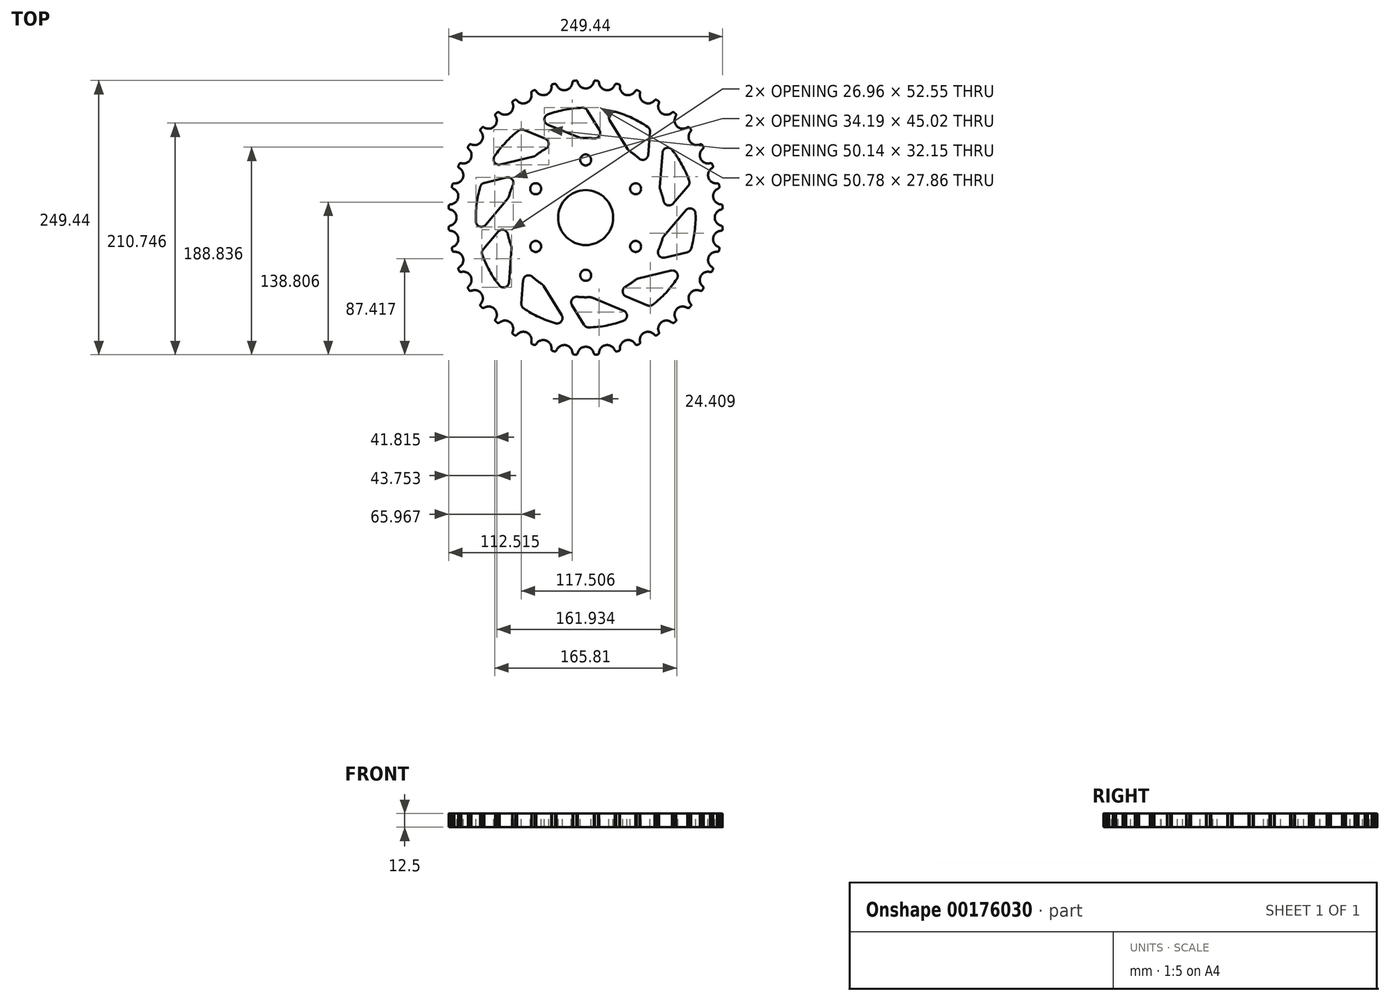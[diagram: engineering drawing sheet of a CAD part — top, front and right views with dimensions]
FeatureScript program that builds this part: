
annotation { "Feature Type Name" : "Feature", "Feature Type Description" : "" }
export const myFeature = defineFeature(function(context is Context, id is Id, definition is map)
    precondition{}
    {
        {
            var Q0;
            Q0=qCreatedBy(makeId("Top.planeOp"),FACE);
            var sketch = newSketch(context, id + "F0", { "sketchPlane" : qUnion([Q0])});
            skCircle(sketch, "E0", {"center": v(0, 0) * mm, "radius": 125 * mm});
            skSolve(sketch);
        }
        {
            var Q0;
            Q0 = qSketchRegion(id + "F0", true);
            extrude(context, id + "F1", {"entities" : qUnion([Q0]), "depth" : 12.5 * mm});
        }
        {
            var Q0;
            Q0=makeQuery(id+"F1.opExtrude","CAP_FACE",FACE,{"disambiguationData":[OSD([sQuery(id+"F0.wireOp",EDGE,"E0")])],"isStart":false});
            var sketch = newSketch(context, id + "F2", { "sketchPlane" : qUnion([Q0])});
            skCircle(sketch, "E1", {"center": v(0, 0) * mm, "radius": 25 * mm});
            skSolve(sketch);
        }
        {
            var Q0;
            Q0 = qSketchRegion(id + "F2", true);
            extrude(context, id + "F3", {"entities" : qUnion([Q0]), "operationType" : NewBodyOperationType.REMOVE, "endBound" : BoundingType.THROUGH_ALL, "oppositeDirection" : true, "depth" : 25 * mm});
        }
        {
            var Q0;
            Q0=makeQuery(id+"F1.opExtrude","CAP_FACE",FACE,{"disambiguationData":[OSD([sQuery(id+"F0.wireOp",EDGE,"E0")])],"isStart":false});
            var sketch = newSketch(context, id + "F4", { "sketchPlane" : qUnion([Q0])});
            skArc(sketch, "E2", {"start": v(-42.76, 30.46) * mm, "mid": v(-45.47, 26.25) * mm, "end": v(-47.76, 21.8) * mm});
            skCircle(sketch, "E3", {"center": v(0, 52.5) * mm, "radius": 5 * mm});
            skCircle(sketch, "E4.1.0", {"center": v(-45.47, 26.25) * mm, "radius": 5 * mm});
            skCircle(sketch, "E4.2.0", {"center": v(-45.47, -26.25) * mm, "radius": 5 * mm});
            skCircle(sketch, "E4.3.0", {"center": v(0, -52.5) * mm, "radius": 5 * mm});
            skCircle(sketch, "E4.4.0", {"center": v(45.47, -26.25) * mm, "radius": 5 * mm});
            skCircle(sketch, "E4.5.0", {"center": v(45.47, 26.25) * mm, "radius": 5 * mm});
            skArc(sketch, "E5.trimOffspring", {"start": v(5, 52.26) * mm, "mid": v(0, 52.5) * mm, "end": v(-5, 52.26) * mm});
            skArc(sketch, "E6.trimOffspring", {"start": v(-47.76, -21.8) * mm, "mid": v(-45.47, -26.25) * mm, "end": v(-42.76, -30.46) * mm});
            skArc(sketch, "E7.trimOffspring", {"start": v(47.76, 21.8) * mm, "mid": v(45.47, 26.25) * mm, "end": v(42.76, 30.46) * mm});
            skArc(sketch, "E8.trimOffspring", {"start": v(42.76, -30.46) * mm, "mid": v(45.47, -26.25) * mm, "end": v(47.76, -21.8) * mm});
            skArc(sketch, "E9.trimOffspring", {"start": v(-5, -52.26) * mm, "mid": v(0, -52.5) * mm, "end": v(5, -52.26) * mm});
            skSolve(sketch);
        }
        {
            var Q0;
            Q0 = qSketchRegion(id + "F4", true);
            extrude(context, id + "F5", {"entities" : qUnion([Q0]), "operationType" : NewBodyOperationType.REMOVE, "endBound" : BoundingType.THROUGH_ALL, "oppositeDirection" : true, "depth" : 25 * mm});
        }
        {
            var Q0;
            Q0=makeQuery(id+"F1.opExtrude","CAP_FACE",FACE,{"disambiguationData":[OSD([sQuery(id+"F0.wireOp",EDGE,"E0")])],"isStart":false});
            var sketch = newSketch(context, id + "F6", { "sketchPlane" : qUnion([Q0])});
            skCircle(sketch, "E10", {"center": v(0, 125) * mm, "radius": 7.5 * mm});
            skCircle(sketch, "E11.1.0", {"center": v(-19.55, 123.46) * mm, "radius": 7.5 * mm});
            skCircle(sketch, "E11.2.0", {"center": v(-38.63, 118.88) * mm, "radius": 7.5 * mm});
            skCircle(sketch, "E11.3.0", {"center": v(-56.75, 111.38) * mm, "radius": 7.5 * mm});
            skCircle(sketch, "E11.4.0", {"center": v(-73.47, 101.13) * mm, "radius": 7.5 * mm});
            skCircle(sketch, "E11.5.0", {"center": v(-88.39, 88.39) * mm, "radius": 7.5 * mm});
            skCircle(sketch, "E11.6.0", {"center": v(-101.13, 73.47) * mm, "radius": 7.5 * mm});
            skCircle(sketch, "E11.7.0", {"center": v(-111.38, 56.75) * mm, "radius": 7.5 * mm});
            skCircle(sketch, "E11.8.0", {"center": v(-118.88, 38.63) * mm, "radius": 7.5 * mm});
            skCircle(sketch, "E11.9.0", {"center": v(-123.46, 19.55) * mm, "radius": 7.5 * mm});
            skCircle(sketch, "E11.10.0", {"center": v(-125, 0) * mm, "radius": 7.5 * mm});
            skCircle(sketch, "E11.11.0", {"center": v(-123.46, -19.55) * mm, "radius": 7.5 * mm});
            skCircle(sketch, "E11.12.0", {"center": v(-118.88, -38.63) * mm, "radius": 7.5 * mm});
            skCircle(sketch, "E11.13.0", {"center": v(-111.38, -56.75) * mm, "radius": 7.5 * mm});
            skCircle(sketch, "E11.14.0", {"center": v(-101.13, -73.47) * mm, "radius": 7.5 * mm});
            skCircle(sketch, "E11.15.0", {"center": v(-88.39, -88.39) * mm, "radius": 7.5 * mm});
            skCircle(sketch, "E11.16.0", {"center": v(-73.47, -101.13) * mm, "radius": 7.5 * mm});
            skCircle(sketch, "E11.17.0", {"center": v(-56.75, -111.38) * mm, "radius": 7.5 * mm});
            skCircle(sketch, "E11.18.0", {"center": v(-38.63, -118.88) * mm, "radius": 7.5 * mm});
            skCircle(sketch, "E11.19.0", {"center": v(-19.55, -123.46) * mm, "radius": 7.5 * mm});
            skCircle(sketch, "E11.20.0", {"center": v(0, -125) * mm, "radius": 7.5 * mm});
            skCircle(sketch, "E11.21.0", {"center": v(19.55, -123.46) * mm, "radius": 7.5 * mm});
            skCircle(sketch, "E11.22.0", {"center": v(38.63, -118.88) * mm, "radius": 7.5 * mm});
            skCircle(sketch, "E11.23.0", {"center": v(56.75, -111.38) * mm, "radius": 7.5 * mm});
            skCircle(sketch, "E11.24.0", {"center": v(73.47, -101.13) * mm, "radius": 7.5 * mm});
            skCircle(sketch, "E11.25.0", {"center": v(88.39, -88.39) * mm, "radius": 7.5 * mm});
            skCircle(sketch, "E11.26.0", {"center": v(101.13, -73.47) * mm, "radius": 7.5 * mm});
            skCircle(sketch, "E11.27.0", {"center": v(111.38, -56.75) * mm, "radius": 7.5 * mm});
            skCircle(sketch, "E11.28.0", {"center": v(118.88, -38.63) * mm, "radius": 7.5 * mm});
            skCircle(sketch, "E11.29.0", {"center": v(123.46, -19.55) * mm, "radius": 7.5 * mm});
            skCircle(sketch, "E11.30.0", {"center": v(125, 0) * mm, "radius": 7.5 * mm});
            skCircle(sketch, "E11.31.0", {"center": v(123.46, 19.55) * mm, "radius": 7.5 * mm});
            skCircle(sketch, "E11.32.0", {"center": v(118.88, 38.63) * mm, "radius": 7.5 * mm});
            skCircle(sketch, "E11.33.0", {"center": v(111.38, 56.75) * mm, "radius": 7.5 * mm});
            skCircle(sketch, "E11.34.0", {"center": v(101.13, 73.47) * mm, "radius": 7.5 * mm});
            skCircle(sketch, "E11.35.0", {"center": v(88.39, 88.39) * mm, "radius": 7.5 * mm});
            skCircle(sketch, "E11.36.0", {"center": v(73.47, 101.13) * mm, "radius": 7.5 * mm});
            skCircle(sketch, "E11.37.0", {"center": v(56.75, 111.38) * mm, "radius": 7.5 * mm});
            skCircle(sketch, "E11.38.0", {"center": v(38.63, 118.88) * mm, "radius": 7.5 * mm});
            skCircle(sketch, "E11.39.0", {"center": v(19.55, 123.46) * mm, "radius": 7.5 * mm});
            skPoint(sketch, "E11.center", {"position": v(0, 0) * mm});
            skSolve(sketch);
        }
        {
            var Q0;
            Q0 = qSketchRegion(id + "F6", true);
            extrude(context, id + "F7", {"entities" : qUnion([Q0]), "operationType" : NewBodyOperationType.REMOVE, "endBound" : BoundingType.THROUGH_ALL, "oppositeDirection" : true, "depth" : 25 * mm});
        }
        {
            var Q0;
            Q0=makeQuery(id+"F1.opExtrude","CAP_FACE",FACE,{"disambiguationData":[OSD([sQuery(id+"F0.wireOp",EDGE,"E0")])],"isStart":false});
            var sketch = newSketch(context, id + "F8", { "sketchPlane" : qUnion([Q0])});
            skArc(sketch, "E12", {"start": v(8.47, 124.7) * mm, "mid": v(7.71, 124.13) * mm, "end": v(7.3, 123.29) * mm});
            skArc(sketch, "E13", {"start": v(12.07, 122.91) * mm, "mid": v(11.8, 123.81) * mm, "end": v(11.15, 124.49) * mm});
            skPoint(sketch, "E14.orphan", {"position": v(7.38, 123.29) * mm});
            skLineSegment(sketch, "E15", {"start": v(8.47, 124.7) * mm, "end": v(7.23, 125.28) * mm});
            skLineSegment(sketch, "E16", {"start": v(7.23, 125.28) * mm, "end": v(7.3, 123.29) * mm});
            skLineSegment(sketch, "E17", {"start": v(11.15, 124.49) * mm, "end": v(12.69, 124.92) * mm});
            skLineSegment(sketch, "E18", {"start": v(12.69, 124.92) * mm, "end": v(12.07, 122.91) * mm});
            skArc(sketch, "E19.1.0", {"start": v(-11.15, 124.49) * mm, "mid": v(-11.8, 123.81) * mm, "end": v(-12.07, 122.91) * mm});
            skLineSegment(sketch, "E19.1.1", {"start": v(-12.46, 124.87) * mm, "end": v(-12.07, 122.91) * mm});
            skLineSegment(sketch, "E19.1.2", {"start": v(-11.15, 124.49) * mm, "end": v(-12.46, 124.87) * mm});
            skLineSegment(sketch, "E19.1.3", {"start": v(-8.47, 124.7) * mm, "end": v(-7, 125.36) * mm});
            skArc(sketch, "E19.1.4", {"start": v(-7.3, 123.29) * mm, "mid": v(-7.71, 124.13) * mm, "end": v(-8.47, 124.7) * mm});
            skLineSegment(sketch, "E19.1.5", {"start": v(-7, 125.36) * mm, "end": v(-7.3, 123.29) * mm});
            skArc(sketch, "E19.2.0", {"start": v(-30.48, 121.21) * mm, "mid": v(-31.02, 120.44) * mm, "end": v(-31.15, 119.5) * mm});
            skLineSegment(sketch, "E19.2.1", {"start": v(-31.84, 121.38) * mm, "end": v(-31.15, 119.5) * mm});
            skLineSegment(sketch, "E19.2.2", {"start": v(-30.48, 121.21) * mm, "end": v(-31.84, 121.38) * mm});
            skLineSegment(sketch, "E19.2.3", {"start": v(-27.87, 121.84) * mm, "end": v(-26.53, 122.72) * mm});
            skArc(sketch, "E19.2.4", {"start": v(-26.5, 120.63) * mm, "mid": v(-27.04, 121.4) * mm, "end": v(-27.87, 121.84) * mm});
            skLineSegment(sketch, "E19.2.5", {"start": v(-26.53, 122.72) * mm, "end": v(-26.5, 120.63) * mm});
            skArc(sketch, "E19.3.0", {"start": v(-49.07, 114.95) * mm, "mid": v(-49.48, 114.1) * mm, "end": v(-49.46, 113.16) * mm});
            skLineSegment(sketch, "E19.3.1", {"start": v(-50.43, 114.9) * mm, "end": v(-49.46, 113.16) * mm});
            skLineSegment(sketch, "E19.3.2", {"start": v(-49.07, 114.95) * mm, "end": v(-50.43, 114.9) * mm});
            skLineSegment(sketch, "E19.3.3", {"start": v(-46.59, 115.98) * mm, "end": v(-45.4, 117.06) * mm});
            skArc(sketch, "E19.3.4", {"start": v(-45.04, 115) * mm, "mid": v(-45.7, 115.67) * mm, "end": v(-46.59, 115.98) * mm});
            skLineSegment(sketch, "E19.3.5", {"start": v(-45.4, 117.06) * mm, "end": v(-45.04, 115) * mm});
            skArc(sketch, "E19.4.0", {"start": v(-66.45, 105.86) * mm, "mid": v(-66.72, 104.96) * mm, "end": v(-66.56, 104.03) * mm});
            skLineSegment(sketch, "E19.4.1", {"start": v(-67.79, 105.6) * mm, "end": v(-66.56, 104.03) * mm});
            skLineSegment(sketch, "E19.4.2", {"start": v(-66.45, 105.86) * mm, "end": v(-67.79, 105.6) * mm});
            skLineSegment(sketch, "E19.4.3", {"start": v(-64.15, 107.26) * mm, "end": v(-63.16, 108.52) * mm});
            skArc(sketch, "E19.4.4", {"start": v(-62.48, 106.53) * mm, "mid": v(-63.23, 107.1) * mm, "end": v(-64.15, 107.26) * mm});
            skLineSegment(sketch, "E19.4.5", {"start": v(-63.16, 108.52) * mm, "end": v(-62.48, 106.53) * mm});
            skArc(sketch, "E19.5.0", {"start": v(-82.19, 94.16) * mm, "mid": v(-82.32, 93.23) * mm, "end": v(-82.01, 92.34) * mm});
            skLineSegment(sketch, "E19.5.1", {"start": v(-83.47, 93.7) * mm, "end": v(-82.01, 92.34) * mm});
            skLineSegment(sketch, "E19.5.2", {"start": v(-82.19, 94.16) * mm, "end": v(-83.47, 93.7) * mm});
            skLineSegment(sketch, "E19.5.3", {"start": v(-80.14, 95.9) * mm, "end": v(-79.36, 97.3) * mm});
            skArc(sketch, "E19.5.4", {"start": v(-78.37, 95.45) * mm, "mid": v(-79.2, 95.9) * mm, "end": v(-80.14, 95.9) * mm});
            skLineSegment(sketch, "E19.5.5", {"start": v(-79.36, 97.3) * mm, "end": v(-78.37, 95.45) * mm});
            skArc(sketch, "E19.6.0", {"start": v(-95.9, 80.14) * mm, "mid": v(-95.9, 79.2) * mm, "end": v(-95.45, 78.37) * mm});
            skLineSegment(sketch, "E19.6.1", {"start": v(-97.1, 79.49) * mm, "end": v(-95.45, 78.37) * mm});
            skLineSegment(sketch, "E19.6.2", {"start": v(-95.9, 80.14) * mm, "end": v(-97.1, 79.49) * mm});
            skLineSegment(sketch, "E19.6.3", {"start": v(-94.16, 82.19) * mm, "end": v(-93.6, 83.7) * mm});
            skArc(sketch, "E19.6.4", {"start": v(-92.34, 82.01) * mm, "mid": v(-93.23, 82.32) * mm, "end": v(-94.16, 82.19) * mm});
            skLineSegment(sketch, "E19.6.5", {"start": v(-93.6, 83.7) * mm, "end": v(-92.34, 82.01) * mm});
            skArc(sketch, "E19.7.0", {"start": v(-107.26, 64.15) * mm, "mid": v(-107.1, 63.23) * mm, "end": v(-106.53, 62.48) * mm});
            skLineSegment(sketch, "E19.7.1", {"start": v(-108.34, 63.32) * mm, "end": v(-106.53, 62.48) * mm});
            skLineSegment(sketch, "E19.7.2", {"start": v(-107.26, 64.15) * mm, "end": v(-108.34, 63.32) * mm});
            skLineSegment(sketch, "E19.7.3", {"start": v(-105.86, 66.45) * mm, "end": v(-105.54, 68.02) * mm});
            skArc(sketch, "E19.7.4", {"start": v(-104.03, 66.56) * mm, "mid": v(-104.96, 66.72) * mm, "end": v(-105.86, 66.45) * mm});
            skLineSegment(sketch, "E19.7.5", {"start": v(-105.54, 68.02) * mm, "end": v(-104.03, 66.56) * mm});
            skArc(sketch, "E19.8.0", {"start": v(-115.98, 46.59) * mm, "mid": v(-115.67, 45.7) * mm, "end": v(-115, 45.04) * mm});
            skLineSegment(sketch, "E19.8.1", {"start": v(-116.92, 45.6) * mm, "end": v(-115, 45.04) * mm});
            skLineSegment(sketch, "E19.8.2", {"start": v(-115.98, 46.59) * mm, "end": v(-116.92, 45.6) * mm});
            skLineSegment(sketch, "E19.8.3", {"start": v(-114.95, 49.07) * mm, "end": v(-114.88, 50.67) * mm});
            skArc(sketch, "E19.8.4", {"start": v(-113.16, 49.46) * mm, "mid": v(-114.1, 49.48) * mm, "end": v(-114.95, 49.07) * mm});
            skLineSegment(sketch, "E19.8.5", {"start": v(-114.88, 50.67) * mm, "end": v(-113.16, 49.46) * mm});
            skArc(sketch, "E19.9.0", {"start": v(-121.84, 27.87) * mm, "mid": v(-121.4, 27.04) * mm, "end": v(-120.63, 26.5) * mm});
            skLineSegment(sketch, "E19.9.1", {"start": v(-122.6, 26.74) * mm, "end": v(-120.63, 26.5) * mm});
            skLineSegment(sketch, "E19.9.2", {"start": v(-121.84, 27.87) * mm, "end": v(-122.6, 26.74) * mm});
            skLineSegment(sketch, "E19.9.3", {"start": v(-121.21, 30.48) * mm, "end": v(-121.4, 32.07) * mm});
            skArc(sketch, "E19.9.4", {"start": v(-119.5, 31.15) * mm, "mid": v(-120.44, 31.02) * mm, "end": v(-121.21, 30.48) * mm});
            skLineSegment(sketch, "E19.9.5", {"start": v(-121.4, 32.07) * mm, "end": v(-119.5, 31.15) * mm});
            skArc(sketch, "E19.10.0", {"start": v(-124.7, 8.47) * mm, "mid": v(-124.13, 7.71) * mm, "end": v(-123.29, 7.3) * mm});
            skLineSegment(sketch, "E19.10.1", {"start": v(-125.28, 7.23) * mm, "end": v(-123.29, 7.3) * mm});
            skLineSegment(sketch, "E19.10.2", {"start": v(-124.7, 8.47) * mm, "end": v(-125.28, 7.23) * mm});
            skLineSegment(sketch, "E19.10.3", {"start": v(-124.49, 11.15) * mm, "end": v(-124.92, 12.69) * mm});
            skArc(sketch, "E19.10.4", {"start": v(-122.91, 12.07) * mm, "mid": v(-123.81, 11.8) * mm, "end": v(-124.49, 11.15) * mm});
            skLineSegment(sketch, "E19.10.5", {"start": v(-124.92, 12.69) * mm, "end": v(-122.91, 12.07) * mm});
            skArc(sketch, "E19.11.0", {"start": v(-124.49, -11.15) * mm, "mid": v(-123.81, -11.8) * mm, "end": v(-122.91, -12.07) * mm});
            skLineSegment(sketch, "E19.11.1", {"start": v(-124.87, -12.46) * mm, "end": v(-122.91, -12.07) * mm});
            skLineSegment(sketch, "E19.11.2", {"start": v(-124.49, -11.15) * mm, "end": v(-124.87, -12.46) * mm});
            skLineSegment(sketch, "E19.11.3", {"start": v(-124.7, -8.47) * mm, "end": v(-125.36, -7) * mm});
            skArc(sketch, "E19.11.4", {"start": v(-123.29, -7.3) * mm, "mid": v(-124.13, -7.71) * mm, "end": v(-124.7, -8.47) * mm});
            skLineSegment(sketch, "E19.11.5", {"start": v(-125.36, -7) * mm, "end": v(-123.29, -7.3) * mm});
            skArc(sketch, "E19.12.0", {"start": v(-121.21, -30.48) * mm, "mid": v(-120.44, -31.02) * mm, "end": v(-119.5, -31.15) * mm});
            skLineSegment(sketch, "E19.12.1", {"start": v(-121.38, -31.84) * mm, "end": v(-119.5, -31.15) * mm});
            skLineSegment(sketch, "E19.12.2", {"start": v(-121.21, -30.48) * mm, "end": v(-121.38, -31.84) * mm});
            skLineSegment(sketch, "E19.12.3", {"start": v(-121.84, -27.87) * mm, "end": v(-122.72, -26.53) * mm});
            skArc(sketch, "E19.12.4", {"start": v(-120.63, -26.5) * mm, "mid": v(-121.4, -27.04) * mm, "end": v(-121.84, -27.87) * mm});
            skLineSegment(sketch, "E19.12.5", {"start": v(-122.72, -26.53) * mm, "end": v(-120.63, -26.5) * mm});
            skArc(sketch, "E19.13.0", {"start": v(-114.95, -49.07) * mm, "mid": v(-114.1, -49.48) * mm, "end": v(-113.16, -49.46) * mm});
            skLineSegment(sketch, "E19.13.1", {"start": v(-114.9, -50.43) * mm, "end": v(-113.16, -49.46) * mm});
            skLineSegment(sketch, "E19.13.2", {"start": v(-114.95, -49.07) * mm, "end": v(-114.9, -50.43) * mm});
            skLineSegment(sketch, "E19.13.3", {"start": v(-115.98, -46.59) * mm, "end": v(-117.06, -45.4) * mm});
            skArc(sketch, "E19.13.4", {"start": v(-115, -45.04) * mm, "mid": v(-115.67, -45.7) * mm, "end": v(-115.98, -46.59) * mm});
            skLineSegment(sketch, "E19.13.5", {"start": v(-117.06, -45.4) * mm, "end": v(-115, -45.04) * mm});
            skArc(sketch, "E19.14.0", {"start": v(-105.86, -66.45) * mm, "mid": v(-104.96, -66.72) * mm, "end": v(-104.03, -66.56) * mm});
            skLineSegment(sketch, "E19.14.1", {"start": v(-105.6, -67.79) * mm, "end": v(-104.03, -66.56) * mm});
            skLineSegment(sketch, "E19.14.2", {"start": v(-105.86, -66.45) * mm, "end": v(-105.6, -67.79) * mm});
            skLineSegment(sketch, "E19.14.3", {"start": v(-107.26, -64.15) * mm, "end": v(-108.52, -63.16) * mm});
            skArc(sketch, "E19.14.4", {"start": v(-106.53, -62.48) * mm, "mid": v(-107.1, -63.23) * mm, "end": v(-107.26, -64.15) * mm});
            skLineSegment(sketch, "E19.14.5", {"start": v(-108.52, -63.16) * mm, "end": v(-106.53, -62.48) * mm});
            skArc(sketch, "E19.15.0", {"start": v(-94.16, -82.19) * mm, "mid": v(-93.23, -82.32) * mm, "end": v(-92.34, -82.01) * mm});
            skLineSegment(sketch, "E19.15.1", {"start": v(-93.7, -83.47) * mm, "end": v(-92.34, -82.01) * mm});
            skLineSegment(sketch, "E19.15.2", {"start": v(-94.16, -82.19) * mm, "end": v(-93.7, -83.47) * mm});
            skLineSegment(sketch, "E19.15.3", {"start": v(-95.9, -80.14) * mm, "end": v(-97.3, -79.36) * mm});
            skArc(sketch, "E19.15.4", {"start": v(-95.45, -78.37) * mm, "mid": v(-95.9, -79.2) * mm, "end": v(-95.9, -80.14) * mm});
            skLineSegment(sketch, "E19.15.5", {"start": v(-97.3, -79.36) * mm, "end": v(-95.45, -78.37) * mm});
            skArc(sketch, "E19.16.0", {"start": v(-80.14, -95.9) * mm, "mid": v(-79.2, -95.9) * mm, "end": v(-78.37, -95.45) * mm});
            skLineSegment(sketch, "E19.16.1", {"start": v(-79.49, -97.1) * mm, "end": v(-78.37, -95.45) * mm});
            skLineSegment(sketch, "E19.16.2", {"start": v(-80.14, -95.9) * mm, "end": v(-79.49, -97.1) * mm});
            skLineSegment(sketch, "E19.16.3", {"start": v(-82.19, -94.16) * mm, "end": v(-83.7, -93.6) * mm});
            skArc(sketch, "E19.16.4", {"start": v(-82.01, -92.34) * mm, "mid": v(-82.32, -93.23) * mm, "end": v(-82.19, -94.16) * mm});
            skLineSegment(sketch, "E19.16.5", {"start": v(-83.7, -93.6) * mm, "end": v(-82.01, -92.34) * mm});
            skArc(sketch, "E19.17.0", {"start": v(-64.15, -107.26) * mm, "mid": v(-63.23, -107.1) * mm, "end": v(-62.48, -106.53) * mm});
            skLineSegment(sketch, "E19.17.1", {"start": v(-63.32, -108.34) * mm, "end": v(-62.48, -106.53) * mm});
            skLineSegment(sketch, "E19.17.2", {"start": v(-64.15, -107.26) * mm, "end": v(-63.32, -108.34) * mm});
            skLineSegment(sketch, "E19.17.3", {"start": v(-66.45, -105.86) * mm, "end": v(-68.02, -105.54) * mm});
            skArc(sketch, "E19.17.4", {"start": v(-66.56, -104.03) * mm, "mid": v(-66.72, -104.96) * mm, "end": v(-66.45, -105.86) * mm});
            skLineSegment(sketch, "E19.17.5", {"start": v(-68.02, -105.54) * mm, "end": v(-66.56, -104.03) * mm});
            skArc(sketch, "E19.18.0", {"start": v(-46.59, -115.98) * mm, "mid": v(-45.7, -115.67) * mm, "end": v(-45.04, -115) * mm});
            skLineSegment(sketch, "E19.18.1", {"start": v(-45.6, -116.92) * mm, "end": v(-45.04, -115) * mm});
            skLineSegment(sketch, "E19.18.2", {"start": v(-46.59, -115.98) * mm, "end": v(-45.6, -116.92) * mm});
            skLineSegment(sketch, "E19.18.3", {"start": v(-49.07, -114.95) * mm, "end": v(-50.67, -114.88) * mm});
            skArc(sketch, "E19.18.4", {"start": v(-49.46, -113.16) * mm, "mid": v(-49.48, -114.1) * mm, "end": v(-49.07, -114.95) * mm});
            skLineSegment(sketch, "E19.18.5", {"start": v(-50.67, -114.88) * mm, "end": v(-49.46, -113.16) * mm});
            skArc(sketch, "E19.19.0", {"start": v(-27.87, -121.84) * mm, "mid": v(-27.04, -121.4) * mm, "end": v(-26.5, -120.63) * mm});
            skLineSegment(sketch, "E19.19.1", {"start": v(-26.74, -122.6) * mm, "end": v(-26.5, -120.63) * mm});
            skLineSegment(sketch, "E19.19.2", {"start": v(-27.87, -121.84) * mm, "end": v(-26.74, -122.6) * mm});
            skLineSegment(sketch, "E19.19.3", {"start": v(-30.48, -121.21) * mm, "end": v(-32.07, -121.4) * mm});
            skArc(sketch, "E19.19.4", {"start": v(-31.15, -119.5) * mm, "mid": v(-31.02, -120.44) * mm, "end": v(-30.48, -121.21) * mm});
            skLineSegment(sketch, "E19.19.5", {"start": v(-32.07, -121.4) * mm, "end": v(-31.15, -119.5) * mm});
            skArc(sketch, "E19.20.0", {"start": v(-8.47, -124.7) * mm, "mid": v(-7.71, -124.13) * mm, "end": v(-7.3, -123.29) * mm});
            skLineSegment(sketch, "E19.20.1", {"start": v(-7.23, -125.28) * mm, "end": v(-7.3, -123.29) * mm});
            skLineSegment(sketch, "E19.20.2", {"start": v(-8.47, -124.7) * mm, "end": v(-7.23, -125.28) * mm});
            skLineSegment(sketch, "E19.20.3", {"start": v(-11.15, -124.49) * mm, "end": v(-12.69, -124.92) * mm});
            skArc(sketch, "E19.20.4", {"start": v(-12.07, -122.91) * mm, "mid": v(-11.8, -123.81) * mm, "end": v(-11.15, -124.49) * mm});
            skLineSegment(sketch, "E19.20.5", {"start": v(-12.69, -124.92) * mm, "end": v(-12.07, -122.91) * mm});
            skArc(sketch, "E19.21.0", {"start": v(11.15, -124.49) * mm, "mid": v(11.8, -123.81) * mm, "end": v(12.07, -122.91) * mm});
            skLineSegment(sketch, "E19.21.1", {"start": v(12.46, -124.87) * mm, "end": v(12.07, -122.91) * mm});
            skLineSegment(sketch, "E19.21.2", {"start": v(11.15, -124.49) * mm, "end": v(12.46, -124.87) * mm});
            skLineSegment(sketch, "E19.21.3", {"start": v(8.47, -124.7) * mm, "end": v(7, -125.36) * mm});
            skArc(sketch, "E19.21.4", {"start": v(7.3, -123.29) * mm, "mid": v(7.71, -124.13) * mm, "end": v(8.47, -124.7) * mm});
            skLineSegment(sketch, "E19.21.5", {"start": v(7, -125.36) * mm, "end": v(7.3, -123.29) * mm});
            skArc(sketch, "E19.22.0", {"start": v(30.48, -121.21) * mm, "mid": v(31.02, -120.44) * mm, "end": v(31.15, -119.5) * mm});
            skLineSegment(sketch, "E19.22.1", {"start": v(31.84, -121.38) * mm, "end": v(31.15, -119.5) * mm});
            skLineSegment(sketch, "E19.22.2", {"start": v(30.48, -121.21) * mm, "end": v(31.84, -121.38) * mm});
            skLineSegment(sketch, "E19.22.3", {"start": v(27.87, -121.84) * mm, "end": v(26.53, -122.72) * mm});
            skArc(sketch, "E19.22.4", {"start": v(26.5, -120.63) * mm, "mid": v(27.04, -121.4) * mm, "end": v(27.87, -121.84) * mm});
            skLineSegment(sketch, "E19.22.5", {"start": v(26.53, -122.72) * mm, "end": v(26.5, -120.63) * mm});
            skArc(sketch, "E19.23.0", {"start": v(49.07, -114.95) * mm, "mid": v(49.48, -114.1) * mm, "end": v(49.46, -113.16) * mm});
            skLineSegment(sketch, "E19.23.1", {"start": v(50.43, -114.9) * mm, "end": v(49.46, -113.16) * mm});
            skLineSegment(sketch, "E19.23.2", {"start": v(49.07, -114.95) * mm, "end": v(50.43, -114.9) * mm});
            skLineSegment(sketch, "E19.23.3", {"start": v(46.59, -115.98) * mm, "end": v(45.4, -117.06) * mm});
            skArc(sketch, "E19.23.4", {"start": v(45.04, -115) * mm, "mid": v(45.7, -115.67) * mm, "end": v(46.59, -115.98) * mm});
            skLineSegment(sketch, "E19.23.5", {"start": v(45.4, -117.06) * mm, "end": v(45.04, -115) * mm});
            skArc(sketch, "E19.24.0", {"start": v(66.45, -105.86) * mm, "mid": v(66.72, -104.96) * mm, "end": v(66.56, -104.03) * mm});
            skLineSegment(sketch, "E19.24.1", {"start": v(67.79, -105.6) * mm, "end": v(66.56, -104.03) * mm});
            skLineSegment(sketch, "E19.24.2", {"start": v(66.45, -105.86) * mm, "end": v(67.79, -105.6) * mm});
            skLineSegment(sketch, "E19.24.3", {"start": v(64.15, -107.26) * mm, "end": v(63.16, -108.52) * mm});
            skArc(sketch, "E19.24.4", {"start": v(62.48, -106.53) * mm, "mid": v(63.23, -107.1) * mm, "end": v(64.15, -107.26) * mm});
            skLineSegment(sketch, "E19.24.5", {"start": v(63.16, -108.52) * mm, "end": v(62.48, -106.53) * mm});
            skArc(sketch, "E19.25.0", {"start": v(82.19, -94.16) * mm, "mid": v(82.32, -93.23) * mm, "end": v(82.01, -92.34) * mm});
            skLineSegment(sketch, "E19.25.1", {"start": v(83.47, -93.7) * mm, "end": v(82.01, -92.34) * mm});
            skLineSegment(sketch, "E19.25.2", {"start": v(82.19, -94.16) * mm, "end": v(83.47, -93.7) * mm});
            skLineSegment(sketch, "E19.25.3", {"start": v(80.14, -95.9) * mm, "end": v(79.36, -97.3) * mm});
            skArc(sketch, "E19.25.4", {"start": v(78.37, -95.45) * mm, "mid": v(79.2, -95.9) * mm, "end": v(80.14, -95.9) * mm});
            skLineSegment(sketch, "E19.25.5", {"start": v(79.36, -97.3) * mm, "end": v(78.37, -95.45) * mm});
            skArc(sketch, "E19.26.0", {"start": v(95.9, -80.14) * mm, "mid": v(95.9, -79.2) * mm, "end": v(95.45, -78.37) * mm});
            skLineSegment(sketch, "E19.26.1", {"start": v(97.1, -79.49) * mm, "end": v(95.45, -78.37) * mm});
            skLineSegment(sketch, "E19.26.2", {"start": v(95.9, -80.14) * mm, "end": v(97.1, -79.49) * mm});
            skLineSegment(sketch, "E19.26.3", {"start": v(94.16, -82.19) * mm, "end": v(93.6, -83.7) * mm});
            skArc(sketch, "E19.26.4", {"start": v(92.34, -82.01) * mm, "mid": v(93.23, -82.32) * mm, "end": v(94.16, -82.19) * mm});
            skLineSegment(sketch, "E19.26.5", {"start": v(93.6, -83.7) * mm, "end": v(92.34, -82.01) * mm});
            skArc(sketch, "E19.27.0", {"start": v(107.26, -64.15) * mm, "mid": v(107.1, -63.23) * mm, "end": v(106.53, -62.48) * mm});
            skLineSegment(sketch, "E19.27.1", {"start": v(108.34, -63.32) * mm, "end": v(106.53, -62.48) * mm});
            skLineSegment(sketch, "E19.27.2", {"start": v(107.26, -64.15) * mm, "end": v(108.34, -63.32) * mm});
            skLineSegment(sketch, "E19.27.3", {"start": v(105.86, -66.45) * mm, "end": v(105.54, -68.02) * mm});
            skArc(sketch, "E19.27.4", {"start": v(104.03, -66.56) * mm, "mid": v(104.96, -66.72) * mm, "end": v(105.86, -66.45) * mm});
            skLineSegment(sketch, "E19.27.5", {"start": v(105.54, -68.02) * mm, "end": v(104.03, -66.56) * mm});
            skArc(sketch, "E19.28.0", {"start": v(115.98, -46.59) * mm, "mid": v(115.67, -45.7) * mm, "end": v(115, -45.04) * mm});
            skLineSegment(sketch, "E19.28.1", {"start": v(116.92, -45.6) * mm, "end": v(115, -45.04) * mm});
            skLineSegment(sketch, "E19.28.2", {"start": v(115.98, -46.59) * mm, "end": v(116.92, -45.6) * mm});
            skLineSegment(sketch, "E19.28.3", {"start": v(114.95, -49.07) * mm, "end": v(114.88, -50.67) * mm});
            skArc(sketch, "E19.28.4", {"start": v(113.16, -49.46) * mm, "mid": v(114.1, -49.48) * mm, "end": v(114.95, -49.07) * mm});
            skLineSegment(sketch, "E19.28.5", {"start": v(114.88, -50.67) * mm, "end": v(113.16, -49.46) * mm});
            skArc(sketch, "E19.29.0", {"start": v(121.84, -27.87) * mm, "mid": v(121.4, -27.04) * mm, "end": v(120.63, -26.5) * mm});
            skLineSegment(sketch, "E19.29.1", {"start": v(122.6, -26.74) * mm, "end": v(120.63, -26.5) * mm});
            skLineSegment(sketch, "E19.29.2", {"start": v(121.84, -27.87) * mm, "end": v(122.6, -26.74) * mm});
            skLineSegment(sketch, "E19.29.3", {"start": v(121.21, -30.48) * mm, "end": v(121.4, -32.07) * mm});
            skArc(sketch, "E19.29.4", {"start": v(119.5, -31.15) * mm, "mid": v(120.44, -31.02) * mm, "end": v(121.21, -30.48) * mm});
            skLineSegment(sketch, "E19.29.5", {"start": v(121.4, -32.07) * mm, "end": v(119.5, -31.15) * mm});
            skArc(sketch, "E19.30.0", {"start": v(124.7, -8.47) * mm, "mid": v(124.13, -7.71) * mm, "end": v(123.29, -7.3) * mm});
            skLineSegment(sketch, "E19.30.1", {"start": v(125.28, -7.23) * mm, "end": v(123.29, -7.3) * mm});
            skLineSegment(sketch, "E19.30.2", {"start": v(124.7, -8.47) * mm, "end": v(125.28, -7.23) * mm});
            skLineSegment(sketch, "E19.30.3", {"start": v(124.49, -11.15) * mm, "end": v(124.92, -12.69) * mm});
            skArc(sketch, "E19.30.4", {"start": v(122.91, -12.07) * mm, "mid": v(123.81, -11.8) * mm, "end": v(124.49, -11.15) * mm});
            skLineSegment(sketch, "E19.30.5", {"start": v(124.92, -12.69) * mm, "end": v(122.91, -12.07) * mm});
            skArc(sketch, "E19.31.0", {"start": v(124.49, 11.15) * mm, "mid": v(123.81, 11.8) * mm, "end": v(122.91, 12.07) * mm});
            skLineSegment(sketch, "E19.31.1", {"start": v(124.87, 12.46) * mm, "end": v(122.91, 12.07) * mm});
            skLineSegment(sketch, "E19.31.2", {"start": v(124.49, 11.15) * mm, "end": v(124.87, 12.46) * mm});
            skLineSegment(sketch, "E19.31.3", {"start": v(124.7, 8.47) * mm, "end": v(125.36, 7) * mm});
            skArc(sketch, "E19.31.4", {"start": v(123.29, 7.3) * mm, "mid": v(124.13, 7.71) * mm, "end": v(124.7, 8.47) * mm});
            skLineSegment(sketch, "E19.31.5", {"start": v(125.36, 7) * mm, "end": v(123.29, 7.3) * mm});
            skArc(sketch, "E19.32.0", {"start": v(121.21, 30.48) * mm, "mid": v(120.44, 31.02) * mm, "end": v(119.5, 31.15) * mm});
            skLineSegment(sketch, "E19.32.1", {"start": v(121.38, 31.84) * mm, "end": v(119.5, 31.15) * mm});
            skLineSegment(sketch, "E19.32.2", {"start": v(121.21, 30.48) * mm, "end": v(121.38, 31.84) * mm});
            skLineSegment(sketch, "E19.32.3", {"start": v(121.84, 27.87) * mm, "end": v(122.72, 26.53) * mm});
            skArc(sketch, "E19.32.4", {"start": v(120.63, 26.5) * mm, "mid": v(121.4, 27.04) * mm, "end": v(121.84, 27.87) * mm});
            skLineSegment(sketch, "E19.32.5", {"start": v(122.72, 26.53) * mm, "end": v(120.63, 26.5) * mm});
            skArc(sketch, "E19.33.0", {"start": v(114.95, 49.07) * mm, "mid": v(114.1, 49.48) * mm, "end": v(113.16, 49.46) * mm});
            skLineSegment(sketch, "E19.33.1", {"start": v(114.9, 50.43) * mm, "end": v(113.16, 49.46) * mm});
            skLineSegment(sketch, "E19.33.2", {"start": v(114.95, 49.07) * mm, "end": v(114.9, 50.43) * mm});
            skLineSegment(sketch, "E19.33.3", {"start": v(115.98, 46.59) * mm, "end": v(117.06, 45.4) * mm});
            skArc(sketch, "E19.33.4", {"start": v(115, 45.04) * mm, "mid": v(115.67, 45.7) * mm, "end": v(115.98, 46.59) * mm});
            skLineSegment(sketch, "E19.33.5", {"start": v(117.06, 45.4) * mm, "end": v(115, 45.04) * mm});
            skArc(sketch, "E19.34.0", {"start": v(105.86, 66.45) * mm, "mid": v(104.96, 66.72) * mm, "end": v(104.03, 66.56) * mm});
            skLineSegment(sketch, "E19.34.1", {"start": v(105.6, 67.79) * mm, "end": v(104.03, 66.56) * mm});
            skLineSegment(sketch, "E19.34.2", {"start": v(105.86, 66.45) * mm, "end": v(105.6, 67.79) * mm});
            skLineSegment(sketch, "E19.34.3", {"start": v(107.26, 64.15) * mm, "end": v(108.52, 63.16) * mm});
            skArc(sketch, "E19.34.4", {"start": v(106.53, 62.48) * mm, "mid": v(107.1, 63.23) * mm, "end": v(107.26, 64.15) * mm});
            skLineSegment(sketch, "E19.34.5", {"start": v(108.52, 63.16) * mm, "end": v(106.53, 62.48) * mm});
            skArc(sketch, "E19.35.0", {"start": v(94.16, 82.19) * mm, "mid": v(93.23, 82.32) * mm, "end": v(92.34, 82.01) * mm});
            skLineSegment(sketch, "E19.35.1", {"start": v(93.7, 83.47) * mm, "end": v(92.34, 82.01) * mm});
            skLineSegment(sketch, "E19.35.2", {"start": v(94.16, 82.19) * mm, "end": v(93.7, 83.47) * mm});
            skLineSegment(sketch, "E19.35.3", {"start": v(95.9, 80.14) * mm, "end": v(97.3, 79.36) * mm});
            skArc(sketch, "E19.35.4", {"start": v(95.45, 78.37) * mm, "mid": v(95.9, 79.2) * mm, "end": v(95.9, 80.14) * mm});
            skLineSegment(sketch, "E19.35.5", {"start": v(97.3, 79.36) * mm, "end": v(95.45, 78.37) * mm});
            skArc(sketch, "E19.36.0", {"start": v(80.14, 95.9) * mm, "mid": v(79.2, 95.9) * mm, "end": v(78.37, 95.45) * mm});
            skLineSegment(sketch, "E19.36.1", {"start": v(79.49, 97.1) * mm, "end": v(78.37, 95.45) * mm});
            skLineSegment(sketch, "E19.36.2", {"start": v(80.14, 95.9) * mm, "end": v(79.49, 97.1) * mm});
            skLineSegment(sketch, "E19.36.3", {"start": v(82.19, 94.16) * mm, "end": v(83.7, 93.6) * mm});
            skArc(sketch, "E19.36.4", {"start": v(82.01, 92.34) * mm, "mid": v(82.32, 93.23) * mm, "end": v(82.19, 94.16) * mm});
            skLineSegment(sketch, "E19.36.5", {"start": v(83.7, 93.6) * mm, "end": v(82.01, 92.34) * mm});
            skArc(sketch, "E19.37.0", {"start": v(64.15, 107.26) * mm, "mid": v(63.23, 107.1) * mm, "end": v(62.48, 106.53) * mm});
            skLineSegment(sketch, "E19.37.1", {"start": v(63.32, 108.34) * mm, "end": v(62.48, 106.53) * mm});
            skLineSegment(sketch, "E19.37.2", {"start": v(64.15, 107.26) * mm, "end": v(63.32, 108.34) * mm});
            skLineSegment(sketch, "E19.37.3", {"start": v(66.45, 105.86) * mm, "end": v(68.02, 105.54) * mm});
            skArc(sketch, "E19.37.4", {"start": v(66.56, 104.03) * mm, "mid": v(66.72, 104.96) * mm, "end": v(66.45, 105.86) * mm});
            skLineSegment(sketch, "E19.37.5", {"start": v(68.02, 105.54) * mm, "end": v(66.56, 104.03) * mm});
            skArc(sketch, "E19.38.0", {"start": v(46.59, 115.98) * mm, "mid": v(45.7, 115.67) * mm, "end": v(45.04, 115) * mm});
            skLineSegment(sketch, "E19.38.1", {"start": v(45.6, 116.92) * mm, "end": v(45.04, 115) * mm});
            skLineSegment(sketch, "E19.38.2", {"start": v(46.59, 115.98) * mm, "end": v(45.6, 116.92) * mm});
            skLineSegment(sketch, "E19.38.3", {"start": v(49.07, 114.95) * mm, "end": v(50.67, 114.88) * mm});
            skArc(sketch, "E19.38.4", {"start": v(49.46, 113.16) * mm, "mid": v(49.48, 114.1) * mm, "end": v(49.07, 114.95) * mm});
            skLineSegment(sketch, "E19.38.5", {"start": v(50.67, 114.88) * mm, "end": v(49.46, 113.16) * mm});
            skArc(sketch, "E19.39.0", {"start": v(27.87, 121.84) * mm, "mid": v(27.04, 121.4) * mm, "end": v(26.5, 120.63) * mm});
            skLineSegment(sketch, "E19.39.1", {"start": v(26.74, 122.6) * mm, "end": v(26.5, 120.63) * mm});
            skLineSegment(sketch, "E19.39.2", {"start": v(27.87, 121.84) * mm, "end": v(26.74, 122.6) * mm});
            skLineSegment(sketch, "E19.39.3", {"start": v(30.48, 121.21) * mm, "end": v(32.07, 121.4) * mm});
            skArc(sketch, "E19.39.4", {"start": v(31.15, 119.5) * mm, "mid": v(31.02, 120.44) * mm, "end": v(30.48, 121.21) * mm});
            skLineSegment(sketch, "E19.39.5", {"start": v(32.07, 121.4) * mm, "end": v(31.15, 119.5) * mm});
            skPoint(sketch, "E19.center", {"position": v(0, 0) * mm});
            skSolve(sketch);
        }
        {
            var Q0;
            Q0 = qSketchRegion(id + "F8", true);
            extrude(context, id + "F9", {"entities" : qUnion([Q0]), "operationType" : NewBodyOperationType.REMOVE, "endBound" : BoundingType.THROUGH_ALL, "oppositeDirection" : true, "depth" : 25 * mm});
        }
        {
            var Q0;
            Q0=makeQuery(id+"F1.opExtrude","CAP_FACE",FACE,{"disambiguationData":[OSD([sQuery(id+"F0.wireOp",EDGE,"E0")])],"isStart":false});
            var sketch = newSketch(context, id + "F10", { "sketchPlane" : qUnion([Q0])});
            skArc(sketch, "E20", {"start": v(-72.37, -4.29) * mm, "mid": v(-70.78, -15.68) * mm, "end": v(-67.42, -26.67) * mm});
            skArc(sketch, "E21", {"start": v(-95.1, -30.9) * mm, "mid": v(-85.25, -52.27) * mm, "end": v(-70.68, -70.74) * mm});
            skLineSegment(sketch, "E22", {"start": v(0, 100) * mm, "end": v(18.29, 70.16) * mm});
            skLineSegment(sketch, "E23", {"start": v(15.6, 98.78) * mm, "end": v(38.86, 61.2) * mm});
            skLineSegment(sketch, "E24.1.0", {"start": v(-58.78, 80.9) * mm, "end": v(-26.44, 67.5) * mm});
            skLineSegment(sketch, "E24.1.1", {"start": v(-45.44, 89.08) * mm, "end": v(-4.53, 72.36) * mm});
            skLineSegment(sketch, "E24.2.0", {"start": v(-95.1, 30.9) * mm, "end": v(-61.07, 39.07) * mm});
            skLineSegment(sketch, "E24.2.1", {"start": v(-89.12, 45.36) * mm, "end": v(-46.2, 55.87) * mm});
            skLineSegment(sketch, "E24.3.0", {"start": v(-95.1, -30.9) * mm, "end": v(-72.37, -4.29) * mm});
            skLineSegment(sketch, "E24.3.1", {"start": v(-98.76, -15.69) * mm, "end": v(-70.22, 18.05) * mm});
            skLineSegment(sketch, "E24.4.0", {"start": v(-58.78, -80.9) * mm, "end": v(-56.03, -46) * mm});
            skLineSegment(sketch, "E24.4.1", {"start": v(-70.68, -70.74) * mm, "end": v(-67.42, -26.67) * mm});
            skLineSegment(sketch, "E24.5.0", {"start": v(0, -100) * mm, "end": v(-18.29, -70.16) * mm});
            skLineSegment(sketch, "E24.5.1", {"start": v(-15.6, -98.78) * mm, "end": v(-38.86, -61.2) * mm});
            skLineSegment(sketch, "E24.6.0", {"start": v(58.78, -80.9) * mm, "end": v(26.44, -67.5) * mm});
            skLineSegment(sketch, "E24.6.1", {"start": v(45.44, -89.08) * mm, "end": v(4.53, -72.36) * mm});
            skLineSegment(sketch, "E24.7.0", {"start": v(95.1, -30.9) * mm, "end": v(61.07, -39.07) * mm});
            skLineSegment(sketch, "E24.7.1", {"start": v(89.12, -45.36) * mm, "end": v(46.2, -55.87) * mm});
            skLineSegment(sketch, "E24.8.0", {"start": v(95.1, 30.9) * mm, "end": v(72.37, 4.29) * mm});
            skLineSegment(sketch, "E24.8.1", {"start": v(98.76, 15.69) * mm, "end": v(70.22, -18.05) * mm});
            skLineSegment(sketch, "E24.9.0", {"start": v(58.78, 80.9) * mm, "end": v(56.03, 46) * mm});
            skLineSegment(sketch, "E24.9.1", {"start": v(70.68, 70.74) * mm, "end": v(67.42, 26.67) * mm});
            skArc(sketch, "E25.trimOffspring", {"start": v(-95.1, 30.9) * mm, "mid": v(-99.7, 7.82) * mm, "end": v(-98.76, -15.69) * mm});
            skArc(sketch, "E26.trimOffspring", {"start": v(-61.07, 39.07) * mm, "mid": v(-66.48, 28.92) * mm, "end": v(-70.22, 18.05) * mm});
            skArc(sketch, "E27.trimOffspring", {"start": v(-58.78, 80.9) * mm, "mid": v(-76.06, 64.93) * mm, "end": v(-89.12, 45.36) * mm});
            skArc(sketch, "E28.trimOffspring", {"start": v(-26.44, 67.5) * mm, "mid": v(-36.78, 62.48) * mm, "end": v(-46.2, 55.87) * mm});
            skArc(sketch, "E29.trimOffspring", {"start": v(0, 100) * mm, "mid": v(-23.37, 97.23) * mm, "end": v(-45.44, 89.08) * mm});
            skArc(sketch, "E30.trimOffspring", {"start": v(18.29, 70.16) * mm, "mid": v(6.96, 72.16) * mm, "end": v(-4.53, 72.36) * mm});
            skArc(sketch, "E31.trimOffspring", {"start": v(58.78, 80.9) * mm, "mid": v(38.25, 92.4) * mm, "end": v(15.6, 98.78) * mm});
            skArc(sketch, "E32.trimOffspring", {"start": v(56.03, 46) * mm, "mid": v(48.05, 54.29) * mm, "end": v(38.86, 61.2) * mm});
            skArc(sketch, "E33.trimOffspring", {"start": v(95.1, 30.9) * mm, "mid": v(85.25, 52.27) * mm, "end": v(70.68, 70.74) * mm});
            skArc(sketch, "E34.trimOffspring", {"start": v(72.37, 4.29) * mm, "mid": v(70.78, 15.68) * mm, "end": v(67.42, 26.67) * mm});
            skArc(sketch, "E35.trimOffspring", {"start": v(95.1, -30.9) * mm, "mid": v(99.7, -7.82) * mm, "end": v(98.76, 15.69) * mm});
            skArc(sketch, "E36.trimOffspring", {"start": v(61.07, -39.07) * mm, "mid": v(66.48, -28.92) * mm, "end": v(70.22, -18.05) * mm});
            skArc(sketch, "E37.trimOffspring", {"start": v(58.78, -80.9) * mm, "mid": v(76.06, -64.93) * mm, "end": v(89.12, -45.36) * mm});
            skArc(sketch, "E38.trimOffspring", {"start": v(26.44, -67.5) * mm, "mid": v(36.78, -62.48) * mm, "end": v(46.2, -55.87) * mm});
            skArc(sketch, "E39.trimOffspring", {"start": v(-18.29, -70.16) * mm, "mid": v(-6.96, -72.16) * mm, "end": v(4.53, -72.36) * mm});
            skArc(sketch, "E40.trimOffspring", {"start": v(0, -100) * mm, "mid": v(23.37, -97.23) * mm, "end": v(45.44, -89.08) * mm});
            skArc(sketch, "E41.trimOffspring", {"start": v(-58.78, -80.9) * mm, "mid": v(-38.25, -92.4) * mm, "end": v(-15.6, -98.78) * mm});
            skArc(sketch, "E42.trimOffspring", {"start": v(-56.03, -46) * mm, "mid": v(-48.05, -54.29) * mm, "end": v(-38.86, -61.2) * mm});
            skSolve(sketch);
        }
        {
            var Q0;
            Q0 = qSketchRegion(id + "F10", true);
            extrude(context, id + "F11", {"entities" : qUnion([Q0]), "operationType" : NewBodyOperationType.REMOVE, "endBound" : BoundingType.THROUGH_ALL, "oppositeDirection" : true, "depth" : 25 * mm});
        }
        {
            var Q0;
            Q0=makeQuery(id+"F11.boolean.opBoolean","COPY",EDGE,{"derivedFrom":makeQuery(id+"F11.opExtrude","SWEPT_EDGE",EDGE,{"disambiguationData":[OSD([sQuery(id+"F10.wireOp",EDGE,"E24.5.1"),sQuery(id+"F10.wireOp",EDGE,"E41.trimOffspring")])]})});
            var Q1;
            Q1=makeQuery(id+"F11.boolean.opBoolean","COPY",EDGE,{"derivedFrom":makeQuery(id+"F11.opExtrude","SWEPT_EDGE",EDGE,{"disambiguationData":[OSD([sQuery(id+"F10.wireOp",EDGE,"E24.4.0"),sQuery(id+"F10.wireOp",EDGE,"E41.trimOffspring")])]})});
            var Q2;
            Q2=makeQuery(id+"F11.boolean.opBoolean","COPY",EDGE,{"derivedFrom":makeQuery(id+"F11.opExtrude","SWEPT_EDGE",EDGE,{"disambiguationData":[OSD([sQuery(id+"F10.wireOp",EDGE,"E24.5.1"),sQuery(id+"F10.wireOp",EDGE,"E42.trimOffspring")])]})});
            var Q3;
            Q3=makeQuery(id+"F11.boolean.opBoolean","COPY",EDGE,{"derivedFrom":makeQuery(id+"F11.opExtrude","SWEPT_EDGE",EDGE,{"disambiguationData":[OSD([sQuery(id+"F10.wireOp",EDGE,"E24.4.0"),sQuery(id+"F10.wireOp",EDGE,"E42.trimOffspring")])]})});
            var Q4;
            Q4=makeQuery(id+"F11.boolean.opBoolean","COPY",EDGE,{"derivedFrom":makeQuery(id+"F11.opExtrude","SWEPT_EDGE",EDGE,{"disambiguationData":[OSD([sQuery(id+"F10.wireOp",EDGE,"E21"),sQuery(id+"F10.wireOp",EDGE,"E24.4.1")])]})});
            var Q5;
            Q5=makeQuery(id+"F11.boolean.opBoolean","COPY",EDGE,{"derivedFrom":makeQuery(id+"F11.opExtrude","SWEPT_EDGE",EDGE,{"disambiguationData":[OSD([sQuery(id+"F10.wireOp",EDGE,"E21"),sQuery(id+"F10.wireOp",EDGE,"E24.3.0")])]})});
            var Q6;
            Q6=makeQuery(id+"F11.boolean.opBoolean","COPY",EDGE,{"derivedFrom":makeQuery(id+"F11.opExtrude","SWEPT_EDGE",EDGE,{"disambiguationData":[OSD([sQuery(id+"F10.wireOp",EDGE,"E20"),sQuery(id+"F10.wireOp",EDGE,"E24.3.0")])]})});
            var Q7;
            Q7=makeQuery(id+"F11.boolean.opBoolean","COPY",EDGE,{"derivedFrom":makeQuery(id+"F11.opExtrude","SWEPT_EDGE",EDGE,{"disambiguationData":[OSD([sQuery(id+"F10.wireOp",EDGE,"E20"),sQuery(id+"F10.wireOp",EDGE,"E24.4.1")])]})});
            var Q8;
            Q8=makeQuery(id+"F11.boolean.opBoolean","COPY",EDGE,{"derivedFrom":makeQuery(id+"F11.opExtrude","SWEPT_EDGE",EDGE,{"disambiguationData":[OSD([sQuery(id+"F10.wireOp",EDGE,"E24.3.1"),sQuery(id+"F10.wireOp",EDGE,"E25.trimOffspring")])]})});
            var Q9;
            Q9=makeQuery(id+"F11.boolean.opBoolean","COPY",EDGE,{"derivedFrom":makeQuery(id+"F11.opExtrude","SWEPT_EDGE",EDGE,{"disambiguationData":[OSD([sQuery(id+"F10.wireOp",EDGE,"E24.3.1"),sQuery(id+"F10.wireOp",EDGE,"E26.trimOffspring")])]})});
            var Q10;
            Q10=makeQuery(id+"F11.boolean.opBoolean","COPY",EDGE,{"derivedFrom":makeQuery(id+"F11.opExtrude","SWEPT_EDGE",EDGE,{"disambiguationData":[OSD([sQuery(id+"F10.wireOp",EDGE,"E24.2.0"),sQuery(id+"F10.wireOp",EDGE,"E26.trimOffspring")])]})});
            var Q11;
            Q11=makeQuery(id+"F11.boolean.opBoolean","COPY",EDGE,{"derivedFrom":makeQuery(id+"F11.opExtrude","SWEPT_EDGE",EDGE,{"disambiguationData":[OSD([sQuery(id+"F10.wireOp",EDGE,"E24.2.0"),sQuery(id+"F10.wireOp",EDGE,"E25.trimOffspring")])]})});
            var Q12;
            Q12=makeQuery(id+"F11.boolean.opBoolean","COPY",EDGE,{"derivedFrom":makeQuery(id+"F11.opExtrude","SWEPT_EDGE",EDGE,{"disambiguationData":[OSD([sQuery(id+"F10.wireOp",EDGE,"E24.2.1"),sQuery(id+"F10.wireOp",EDGE,"E27.trimOffspring")])]})});
            var Q13;
            Q13=makeQuery(id+"F11.boolean.opBoolean","COPY",EDGE,{"derivedFrom":makeQuery(id+"F11.opExtrude","SWEPT_EDGE",EDGE,{"disambiguationData":[OSD([sQuery(id+"F10.wireOp",EDGE,"E24.2.1"),sQuery(id+"F10.wireOp",EDGE,"E28.trimOffspring")])]})});
            var Q14;
            Q14=makeQuery(id+"F11.boolean.opBoolean","COPY",EDGE,{"derivedFrom":makeQuery(id+"F11.opExtrude","SWEPT_EDGE",EDGE,{"disambiguationData":[OSD([sQuery(id+"F10.wireOp",EDGE,"E24.1.0"),sQuery(id+"F10.wireOp",EDGE,"E28.trimOffspring")])]})});
            var Q15;
            Q15=makeQuery(id+"F11.boolean.opBoolean","COPY",EDGE,{"derivedFrom":makeQuery(id+"F11.opExtrude","SWEPT_EDGE",EDGE,{"disambiguationData":[OSD([sQuery(id+"F10.wireOp",EDGE,"E24.1.0"),sQuery(id+"F10.wireOp",EDGE,"E27.trimOffspring")])]})});
            var Q16;
            Q16=makeQuery(id+"F11.boolean.opBoolean","COPY",EDGE,{"derivedFrom":makeQuery(id+"F11.opExtrude","SWEPT_EDGE",EDGE,{"disambiguationData":[OSD([sQuery(id+"F10.wireOp",EDGE,"E24.1.1"),sQuery(id+"F10.wireOp",EDGE,"E29.trimOffspring")])]})});
            var Q17;
            Q17=makeQuery(id+"F11.boolean.opBoolean","COPY",EDGE,{"derivedFrom":makeQuery(id+"F11.opExtrude","SWEPT_EDGE",EDGE,{"disambiguationData":[OSD([sQuery(id+"F10.wireOp",EDGE,"E24.1.1"),sQuery(id+"F10.wireOp",EDGE,"E30.trimOffspring")])]})});
            var Q18;
            Q18=makeQuery(id+"F11.boolean.opBoolean","COPY",EDGE,{"derivedFrom":makeQuery(id+"F11.opExtrude","SWEPT_EDGE",EDGE,{"disambiguationData":[OSD([sQuery(id+"F10.wireOp",EDGE,"E22"),sQuery(id+"F10.wireOp",EDGE,"E30.trimOffspring")])]})});
            var Q19;
            Q19=makeQuery(id+"F11.boolean.opBoolean","COPY",EDGE,{"derivedFrom":makeQuery(id+"F11.opExtrude","SWEPT_EDGE",EDGE,{"disambiguationData":[OSD([sQuery(id+"F10.wireOp",EDGE,"E22"),sQuery(id+"F10.wireOp",EDGE,"E29.trimOffspring")])]})});
            var Q20;
            Q20=makeQuery(id+"F11.boolean.opBoolean","COPY",EDGE,{"derivedFrom":makeQuery(id+"F11.opExtrude","SWEPT_EDGE",EDGE,{"disambiguationData":[OSD([sQuery(id+"F10.wireOp",EDGE,"E23"),sQuery(id+"F10.wireOp",EDGE,"E31.trimOffspring")])]})});
            var Q21;
            Q21=makeQuery(id+"F11.boolean.opBoolean","COPY",EDGE,{"derivedFrom":makeQuery(id+"F11.opExtrude","SWEPT_EDGE",EDGE,{"disambiguationData":[OSD([sQuery(id+"F10.wireOp",EDGE,"E23"),sQuery(id+"F10.wireOp",EDGE,"E32.trimOffspring")])]})});
            var Q22;
            Q22=makeQuery(id+"F11.boolean.opBoolean","COPY",EDGE,{"derivedFrom":makeQuery(id+"F11.opExtrude","SWEPT_EDGE",EDGE,{"disambiguationData":[OSD([sQuery(id+"F10.wireOp",EDGE,"E24.9.0"),sQuery(id+"F10.wireOp",EDGE,"E32.trimOffspring")])]})});
            var Q23;
            Q23=makeQuery(id+"F11.boolean.opBoolean","COPY",EDGE,{"derivedFrom":makeQuery(id+"F11.opExtrude","SWEPT_EDGE",EDGE,{"disambiguationData":[OSD([sQuery(id+"F10.wireOp",EDGE,"E24.9.0"),sQuery(id+"F10.wireOp",EDGE,"E31.trimOffspring")])]})});
            var Q24;
            Q24=makeQuery(id+"F11.boolean.opBoolean","COPY",EDGE,{"derivedFrom":makeQuery(id+"F11.opExtrude","SWEPT_EDGE",EDGE,{"disambiguationData":[OSD([sQuery(id+"F10.wireOp",EDGE,"E24.9.1"),sQuery(id+"F10.wireOp",EDGE,"E33.trimOffspring")])]})});
            var Q25;
            Q25=makeQuery(id+"F11.boolean.opBoolean","COPY",EDGE,{"derivedFrom":makeQuery(id+"F11.opExtrude","SWEPT_EDGE",EDGE,{"disambiguationData":[OSD([sQuery(id+"F10.wireOp",EDGE,"E24.9.1"),sQuery(id+"F10.wireOp",EDGE,"E34.trimOffspring")])]})});
            var Q26;
            Q26=makeQuery(id+"F11.boolean.opBoolean","COPY",EDGE,{"derivedFrom":makeQuery(id+"F11.opExtrude","SWEPT_EDGE",EDGE,{"disambiguationData":[OSD([sQuery(id+"F10.wireOp",EDGE,"E24.8.0"),sQuery(id+"F10.wireOp",EDGE,"E34.trimOffspring")])]})});
            var Q27;
            Q27=makeQuery(id+"F11.boolean.opBoolean","COPY",EDGE,{"derivedFrom":makeQuery(id+"F11.opExtrude","SWEPT_EDGE",EDGE,{"disambiguationData":[OSD([sQuery(id+"F10.wireOp",EDGE,"E24.8.0"),sQuery(id+"F10.wireOp",EDGE,"E33.trimOffspring")])]})});
            var Q28;
            Q28=makeQuery(id+"F11.boolean.opBoolean","COPY",EDGE,{"derivedFrom":makeQuery(id+"F11.opExtrude","SWEPT_EDGE",EDGE,{"disambiguationData":[OSD([sQuery(id+"F10.wireOp",EDGE,"E24.8.1"),sQuery(id+"F10.wireOp",EDGE,"E36.trimOffspring")])]})});
            var Q29;
            Q29=makeQuery(id+"F11.boolean.opBoolean","COPY",EDGE,{"derivedFrom":makeQuery(id+"F11.opExtrude","SWEPT_EDGE",EDGE,{"disambiguationData":[OSD([sQuery(id+"F10.wireOp",EDGE,"E24.8.1"),sQuery(id+"F10.wireOp",EDGE,"E35.trimOffspring")])]})});
            var Q30;
            Q30=makeQuery(id+"F11.boolean.opBoolean","COPY",EDGE,{"derivedFrom":makeQuery(id+"F11.opExtrude","SWEPT_EDGE",EDGE,{"disambiguationData":[OSD([sQuery(id+"F10.wireOp",EDGE,"E24.7.0"),sQuery(id+"F10.wireOp",EDGE,"E35.trimOffspring")])]})});
            var Q31;
            Q31=makeQuery(id+"F11.boolean.opBoolean","COPY",EDGE,{"derivedFrom":makeQuery(id+"F11.opExtrude","SWEPT_EDGE",EDGE,{"disambiguationData":[OSD([sQuery(id+"F10.wireOp",EDGE,"E24.7.0"),sQuery(id+"F10.wireOp",EDGE,"E36.trimOffspring")])]})});
            var Q32;
            Q32=makeQuery(id+"F11.boolean.opBoolean","COPY",EDGE,{"derivedFrom":makeQuery(id+"F11.opExtrude","SWEPT_EDGE",EDGE,{"disambiguationData":[OSD([sQuery(id+"F10.wireOp",EDGE,"E24.7.1"),sQuery(id+"F10.wireOp",EDGE,"E37.trimOffspring")])]})});
            var Q33;
            Q33=makeQuery(id+"F11.boolean.opBoolean","COPY",EDGE,{"derivedFrom":makeQuery(id+"F11.opExtrude","SWEPT_EDGE",EDGE,{"disambiguationData":[OSD([sQuery(id+"F10.wireOp",EDGE,"E24.7.1"),sQuery(id+"F10.wireOp",EDGE,"E38.trimOffspring")])]})});
            var Q34;
            Q34=makeQuery(id+"F11.boolean.opBoolean","COPY",EDGE,{"derivedFrom":makeQuery(id+"F11.opExtrude","SWEPT_EDGE",EDGE,{"disambiguationData":[OSD([sQuery(id+"F10.wireOp",EDGE,"E24.6.0"),sQuery(id+"F10.wireOp",EDGE,"E38.trimOffspring")])]})});
            var Q35;
            Q35=makeQuery(id+"F11.boolean.opBoolean","COPY",EDGE,{"derivedFrom":makeQuery(id+"F11.opExtrude","SWEPT_EDGE",EDGE,{"disambiguationData":[OSD([sQuery(id+"F10.wireOp",EDGE,"E24.6.0"),sQuery(id+"F10.wireOp",EDGE,"E37.trimOffspring")])]})});
            var Q36;
            Q36=makeQuery(id+"F11.boolean.opBoolean","COPY",EDGE,{"derivedFrom":makeQuery(id+"F11.opExtrude","SWEPT_EDGE",EDGE,{"disambiguationData":[OSD([sQuery(id+"F10.wireOp",EDGE,"E24.6.1"),sQuery(id+"F10.wireOp",EDGE,"E40.trimOffspring")])]})});
            var Q37;
            Q37=makeQuery(id+"F11.boolean.opBoolean","COPY",EDGE,{"derivedFrom":makeQuery(id+"F11.opExtrude","SWEPT_EDGE",EDGE,{"disambiguationData":[OSD([sQuery(id+"F10.wireOp",EDGE,"E24.6.1"),sQuery(id+"F10.wireOp",EDGE,"E39.trimOffspring")])]})});
            var Q38;
            Q38=makeQuery(id+"F11.boolean.opBoolean","COPY",EDGE,{"derivedFrom":makeQuery(id+"F11.opExtrude","SWEPT_EDGE",EDGE,{"disambiguationData":[OSD([sQuery(id+"F10.wireOp",EDGE,"E24.5.0"),sQuery(id+"F10.wireOp",EDGE,"E39.trimOffspring")])]})});
            var Q39;
            Q39=makeQuery(id+"F11.boolean.opBoolean","COPY",EDGE,{"derivedFrom":makeQuery(id+"F11.opExtrude","SWEPT_EDGE",EDGE,{"disambiguationData":[OSD([sQuery(id+"F10.wireOp",EDGE,"E24.5.0"),sQuery(id+"F10.wireOp",EDGE,"E40.trimOffspring")])]})});
            fillet(context, id + "F12", {"entities" : qUnion([Q0, Q1, Q2, Q3, Q4, Q5, Q6, Q7, Q8, Q9, Q10, Q11, Q12, Q13, Q14, Q15, Q16, Q17, Q18, Q19, Q20, Q21, Q22, Q23, Q24, Q25, Q26, Q27, Q28, Q29, Q30, Q31, Q32, Q33, Q34, Q35, Q36, Q37, Q38, Q39]), "radius" : 5 * mm, "tangentPropagation" : true, "allowEdgeOverflow" : false});
        }
    });
